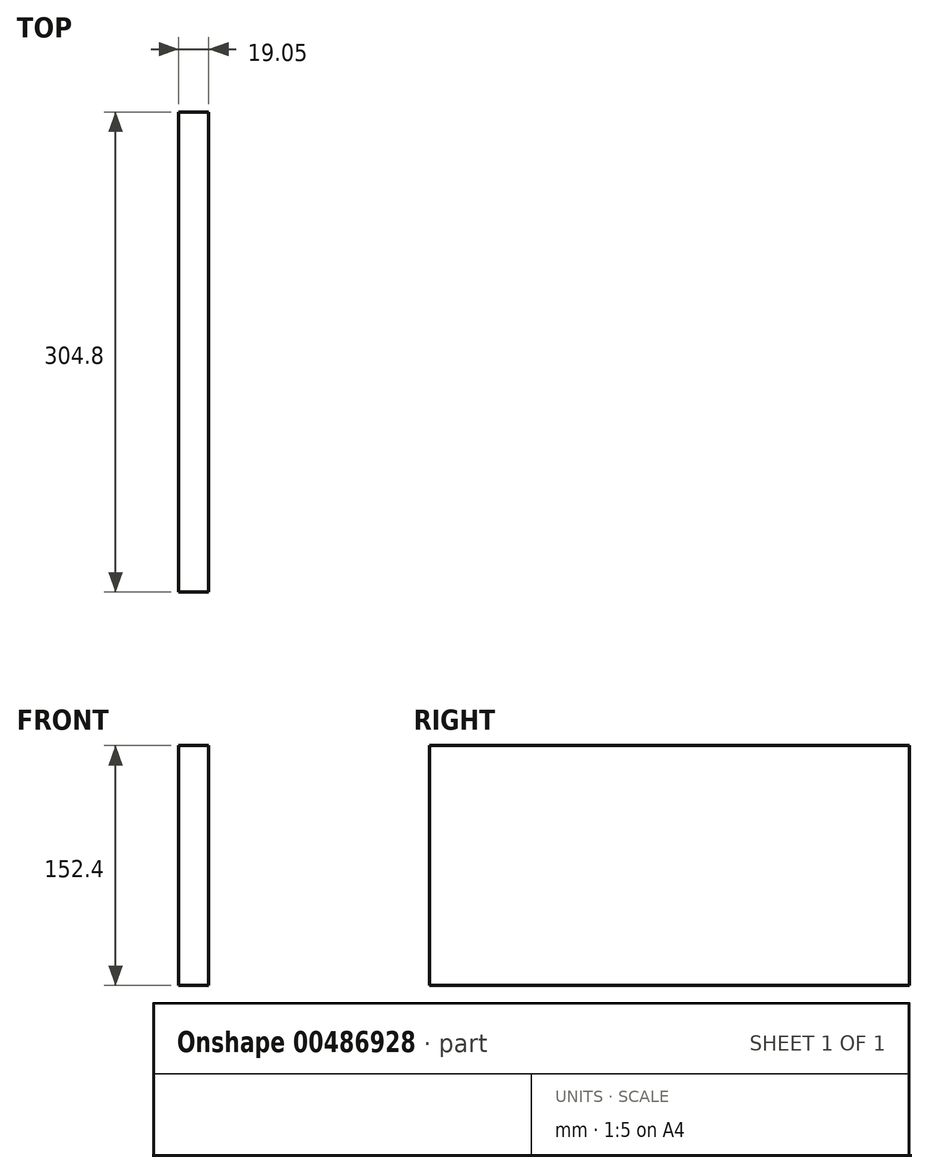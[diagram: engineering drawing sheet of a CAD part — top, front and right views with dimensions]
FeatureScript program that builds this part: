
annotation { "Feature Type Name" : "Feature", "Feature Type Description" : "" }
export const myFeature = defineFeature(function(context is Context, id is Id, definition is map)
    precondition{}
    {
        {
            var Q0;
            Q0=qCreatedBy(makeId("Right.planeOp"),FACE);
            var sketch = newSketch(context, id + "F0", { "sketchPlane" : qUnion([Q0])});
            skLineSegment(sketch, "E0.bottom", {"start": v(-166.66, -72.1) * mm, "end": v(138.14, -72.1) * mm});
            skLineSegment(sketch, "E0.top", {"start": v(-166.66, -224.5) * mm, "end": v(138.14, -224.5) * mm});
            skLineSegment(sketch, "E0.left", {"start": v(-166.66, -72.1) * mm, "end": v(-166.66, -224.5) * mm});
            skLineSegment(sketch, "E0.right", {"start": v(138.14, -72.1) * mm, "end": v(138.14, -224.5) * mm});
            skSolve(sketch);
        }
        {
            var Q0;
            Q0 = qSketchRegion(id + "F0", true);
            extrude(context, id + "F1", {"entities" : qUnion([Q0]), "depth" : 19.05 * mm});
        }
    });
